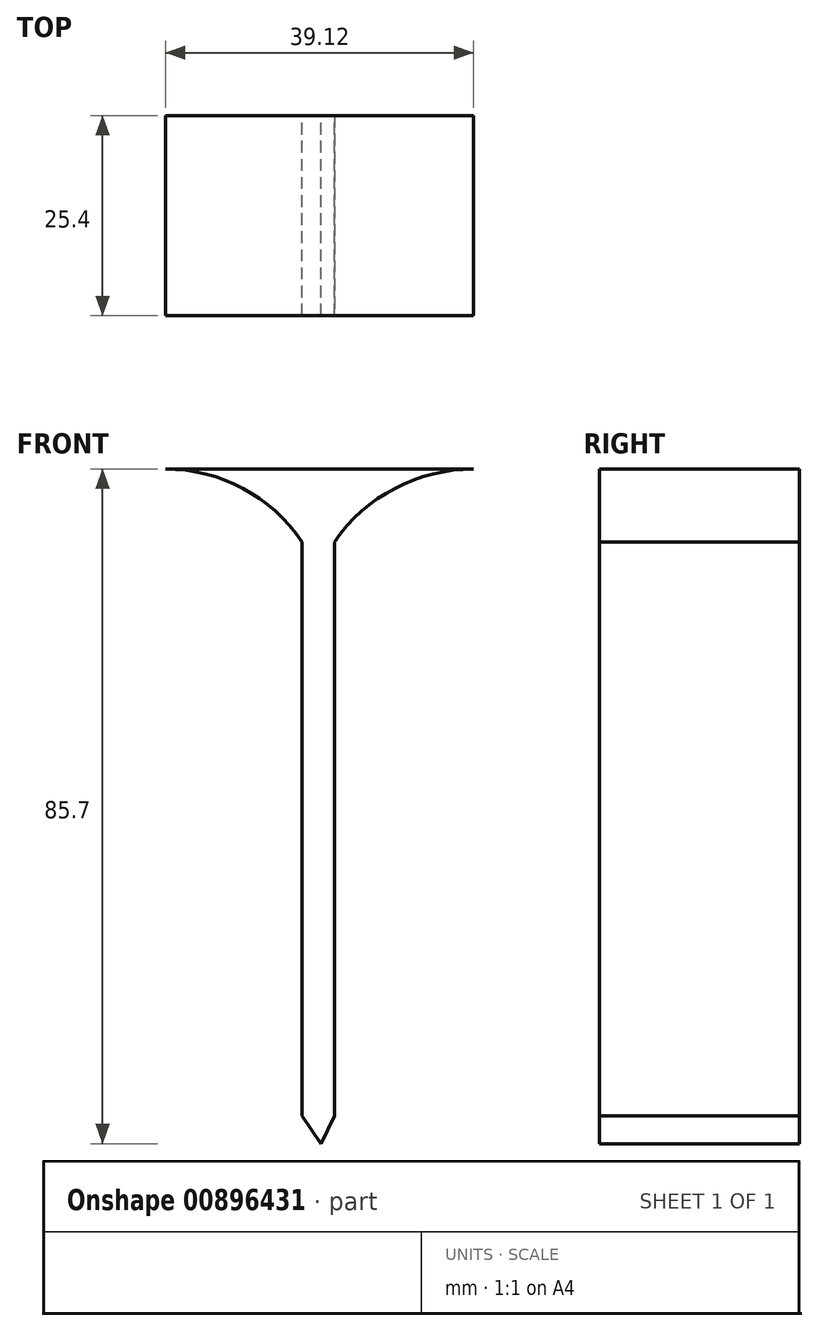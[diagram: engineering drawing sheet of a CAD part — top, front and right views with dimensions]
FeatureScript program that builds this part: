
annotation { "Feature Type Name" : "Feature", "Feature Type Description" : "" }
export const myFeature = defineFeature(function(context is Context, id is Id, definition is map)
    precondition{}
    {
        {
            var Q0;
            Q0=qCreatedBy(makeId("Front.planeOp"),FACE);
            var sketch = newSketch(context, id + "F0", { "sketchPlane" : qUnion([Q0])});
            skLineSegment(sketch, "E0.top", {"start": v(-2.43, -46.88) * mm, "end": v(1.72, -46.88) * mm});
            skLineSegment(sketch, "E0.left", {"start": v(-2.43, 26.02) * mm, "end": v(-2.43, -46.88) * mm});
            skLineSegment(sketch, "E0.right", {"start": v(1.72, 26) * mm, "end": v(1.72, -46.88) * mm});
            skLineSegment(sketch, "E1", {"start": v(-2.43, -46.88) * mm, "end": v(0, -50.44) * mm});
            skLineSegment(sketch, "E2", {"start": v(0, -50.44) * mm, "end": v(1.72, -46.88) * mm});
            skLineSegment(sketch, "E3", {"start": v(-19.74, 35.26) * mm, "end": v(19.38, 35.26) * mm});
            skArc(sketch, "E4", {"start": v(-2.43, 26.02) * mm, "mid": v(-9.93, 32.8) * mm, "end": v(-19.74, 35.26) * mm});
            skArc(sketch, "E5", {"start": v(19.38, 35.26) * mm, "mid": v(9.4, 32.8) * mm, "end": v(1.72, 26) * mm});
            skLineSegment(sketch, "E6", {"start": v(1.72, 26) * mm, "end": v(-2.43, 26.02) * mm});
            skSolve(sketch);
        }
        {
            var Q0;
            Q0 = qSketchRegion(id + "F0", true);
            extrude(context, id + "F1", {"entities" : qUnion([Q0]), "depth" : 25.4 * mm, "offsetDistance" : 25.4 * mm});
        }
    });
